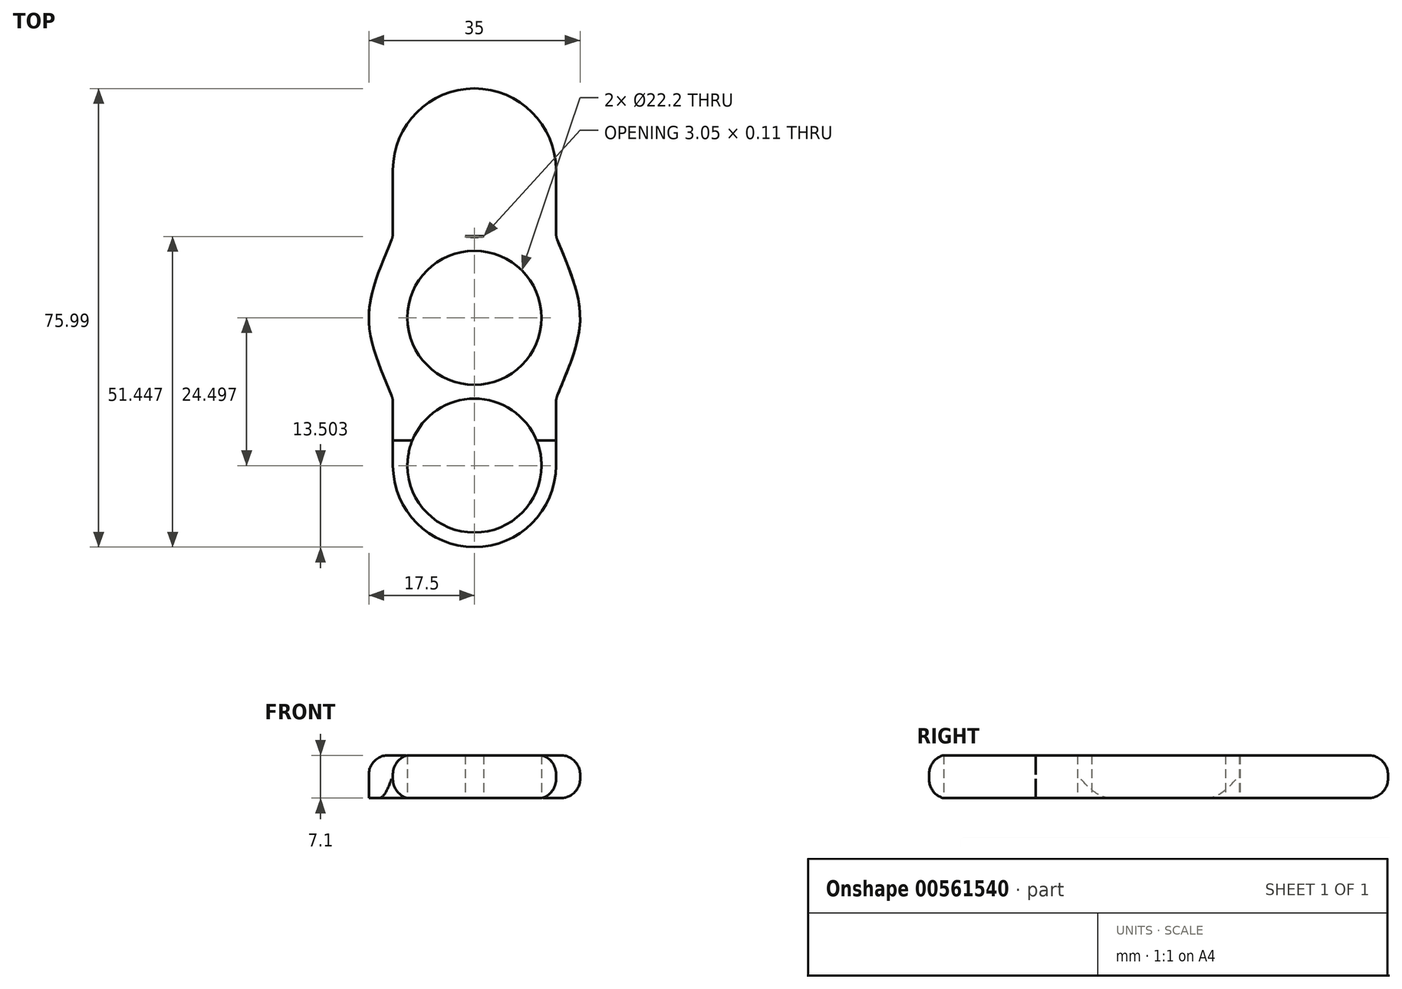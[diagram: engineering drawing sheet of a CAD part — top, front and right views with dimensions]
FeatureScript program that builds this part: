
annotation { "Feature Type Name" : "Feature", "Feature Type Description" : "" }
export const myFeature = defineFeature(function(context is Context, id is Id, definition is map)
    precondition{}
    {
        {
            var Q0;
            Q0=qCreatedBy(makeId("Top.planeOp"),FACE);
            var sketch = newSketch(context, id + "F0", { "sketchPlane" : qUnion([Q0])});
            skCircle(sketch, "E0", {"center": v(0, 0) * mm, "radius": 11.1 * mm});
            skCircle(sketch, "E1.cCircle", {"center": v(0, 0) * mm, "radius": 13.5 * mm, "construction": true});
            skLineSegment(sketch, "E1.0", {"start": v(13.5, 13.5) * mm, "end": v(13.5, -13.5) * mm});
            skLineSegment(sketch, "E1.1", {"start": v(13.5, -13.5) * mm, "end": v(-13.5, -13.5) * mm});
            skLineSegment(sketch, "E1.2", {"start": v(-13.5, -13.5) * mm, "end": v(-13.5, 13.5) * mm});
            skLineSegment(sketch, "E1.3", {"start": v(-13.5, 13.5) * mm, "end": v(13.5, 13.5) * mm});
            skPoint(sketch, "E1.0.midPoint", {"position": v(13.5, 0) * mm});
            skCircle(sketch, "E2", {"center": v(0, 24.5) * mm, "radius": 11.1 * mm});
            skPoint(sketch, "E2.centerSnap0", {"position": v(0, 13.5) * mm});
            skCircle(sketch, "E3", {"center": v(0, -24.5) * mm, "radius": 11.1 * mm});
            skLineSegment(sketch, "E4.top", {"start": v(-13.5, 24.5) * mm, "end": v(13.5, 24.5) * mm});
            skLineSegment(sketch, "E4.left", {"start": v(-13.5, 13.5) * mm, "end": v(-13.5, 24.5) * mm});
            skLineSegment(sketch, "E4.right", {"start": v(13.5, 13.5) * mm, "end": v(13.5, 24.5) * mm});
            skLineSegment(sketch, "E5.bottom", {"start": v(-13.5, -13.5) * mm, "end": v(13.5, -13.5) * mm});
            skLineSegment(sketch, "E5.top", {"start": v(-13.5, -24.5) * mm, "end": v(13.5, -24.5) * mm});
            skLineSegment(sketch, "E5.left", {"start": v(-13.5, -13.5) * mm, "end": v(-13.5, -24.5) * mm});
            skLineSegment(sketch, "E5.right", {"start": v(13.5, -13.5) * mm, "end": v(13.5, -24.5) * mm});
            skArc(sketch, "E6", {"start": v(-13.5, -24.5) * mm, "mid": v(0, -38) * mm, "end": v(13.5, -24.5) * mm});
            skArc(sketch, "E7", {"start": v(13.5, 24.5) * mm, "mid": v(0, 38) * mm, "end": v(-13.5, 24.5) * mm});
            skFitSpline(sketch, "E8", {"points": [v(13.5, 13.5) * mm, v(17.5, 0) * mm, v(13.5, -13.5) * mm], "startDerivative": vector(10.46, -27) * mm, "endDerivative": vector(-10.46, -27) * mm});
            skFitSpline(sketch, "E9", {"points": [v(-13.5, 13.5) * mm, v(-17.5, 0) * mm, v(-13.5, -13.5) * mm], "startDerivative": vector(-10.46, -27) * mm, "endDerivative": vector(10.46, -27) * mm});
            skSolve(sketch);
        }
        {
            var Q0;
            {var subQ4=sQuery(id+"F0.wireOp",EDGE,"E7");Q0=makeQuery(id+"F0.imprint","IMPRINT",FACE,{"disambiguationData":[TD([[makeQuery(id+"F0.imprint","IMPRINT",EDGE,{"derivedFrom":subQ4}),1.0]])]});}
            var Q1;
            {var subQ5=sQuery(id+"F0.wireOp",EDGE,"E4.left");Q1=makeQuery(id+"F0.imprint","IMPRINT",FACE,{"disambiguationData":[TD([[makeQuery(id+"F0.imprint","IMPRINT",EDGE,{"derivedFrom":subQ5}),-1.0]])]});}
            var Q2;
            {var subQ5=sQuery(id+"F0.wireOp",EDGE,"E4.right");Q2=makeQuery(id+"F0.imprint","IMPRINT",FACE,{"disambiguationData":[TD([[makeQuery(id+"F0.imprint","IMPRINT",EDGE,{"derivedFrom":subQ5}),1.0]])]});}
            var Q3;
            Q3=makeQuery(id+"F0.imprint","IMPRINT",FACE,{"disambiguationData":[TD([[makeQuery(id+"F0.imprint","IMPRINT",EDGE,{"derivedFrom":sQuery(id+"F0.wireOp",EDGE,"E0")}),-1.0]])]});
            var Q4;
            Q4=makeQuery(id+"F0.imprint","IMPRINT",FACE,{"disambiguationData":[TD([[makeQuery(id+"F0.imprint","IMPRINT",EDGE,{"derivedFrom":sQuery(id+"F0.wireOp",EDGE,"E1.0")}),1.0]])]});
            var Q5;
            Q5=makeQuery(id+"F0.imprint","IMPRINT",FACE,{"disambiguationData":[TD([[makeQuery(id+"F0.imprint","IMPRINT",EDGE,{"derivedFrom":sQuery(id+"F0.wireOp",EDGE,"E1.2")}),1.0]])]});
            var Q6;
            {var subQ5=sQuery(id+"F0.wireOp",EDGE,"E5.left");Q6=makeQuery(id+"F0.imprint","IMPRINT",FACE,{"disambiguationData":[TD([[makeQuery(id+"F0.imprint","IMPRINT",EDGE,{"derivedFrom":subQ5}),1.0]])]});}
            var Q7;
            {var subQ5=sQuery(id+"F0.wireOp",EDGE,"E5.right");Q7=makeQuery(id+"F0.imprint","IMPRINT",FACE,{"disambiguationData":[TD([[makeQuery(id+"F0.imprint","IMPRINT",EDGE,{"derivedFrom":subQ5}),-1.0]])]});}
            var Q8;
            {var subQ4=sQuery(id+"F0.wireOp",EDGE,"E6");Q8=makeQuery(id+"F0.imprint","IMPRINT",FACE,{"disambiguationData":[TD([[makeQuery(id+"F0.imprint","IMPRINT",EDGE,{"derivedFrom":subQ4}),1.0]])]});}
            var Q9;
            {var subQ0=sQuery(id+"F0.wireOp",EDGE,"E4.top");var subQ1=sQuery(id+"F0.wireOp",EDGE,"E2");var subQ2=makeQuery(id+"F0.imprint","INTERSECT",VERTEX,{"disambiguationData":[OD(0.0)],"derivedFrom":[subQ1,subQ0]});Q9=makeQuery(id+"F0.imprint","IMPRINT",FACE,{"disambiguationData":[TD([[makeQuery(id+"F0.imprint","IMPRINT",EDGE,{"disambiguationData":[TD([[subQ2,1.0]])],"derivedFrom":subQ1}),1.0]])]});}
            var Q10;
            {var subQ0=sQuery(id+"F0.wireOp",EDGE,"E4.top");var subQ1=sQuery(id+"F0.wireOp",EDGE,"E2");var subQ2=makeQuery(id+"F0.imprint","INTERSECT",VERTEX,{"disambiguationData":[OD(0.0)],"derivedFrom":[subQ1,subQ0]});Q10=makeQuery(id+"F0.imprint","IMPRINT",FACE,{"disambiguationData":[TD([[makeQuery(id+"F0.imprint","IMPRINT",EDGE,{"disambiguationData":[TD([[subQ2,-1.0]])],"derivedFrom":subQ1}),1.0]])]});}
            var Q11;
            {var subQ0=sQuery(id+"F0.wireOp",EDGE,"E1.3");var subQ1=sQuery(id+"F0.wireOp",EDGE,"E2");var subQ2=makeQuery(id+"F0.imprint","INTERSECT",VERTEX,{"disambiguationData":[OD(0.0)],"derivedFrom":[subQ1,subQ0]});Q11=makeQuery(id+"F0.imprint","IMPRINT",FACE,{"disambiguationData":[TD([[makeQuery(id+"F0.imprint","IMPRINT",EDGE,{"disambiguationData":[TD([[subQ2,-1.0]])],"derivedFrom":subQ1}),1.0]])]});}
            extrude(context, id + "F1", {"entities" : qUnion([Q0, Q1, Q2, Q3, Q4, Q5, Q6, Q7, Q8, Q9, Q10, Q11]), "depth" : 7.1 * mm, "offsetDistance" : 25 * mm});
        }
        {
            var Q0;
            Q0=makeQuery(id+"F1.opExtrude","SWEPT_EDGE",EDGE,{"disambiguationData":[OSD([sQuery(id+"F0.wireOp",EDGE,"E1.0"),sQuery(id+"F0.wireOp",EDGE,"E5.bottom"),sQuery(id+"F0.wireOp",EDGE,"E5.right"),sQuery(id+"F0.wireOp",EDGE,"E8")])]});
            var Q1;
            Q1=makeQuery(id+"F1.opExtrude","CAP_EDGE",EDGE,{"disambiguationData":[OSD([sQuery(id+"F0.wireOp",EDGE,"E8")])],"isStart":false});
            var Q2;
            Q2=makeQuery(id+"F1.opExtrude","CAP_EDGE",EDGE,{"disambiguationData":[OSD([sQuery(id+"F0.wireOp",EDGE,"E8")])],"isStart":true});
            var Q3;
            Q3=makeQuery(id+"F1.opExtrude","SWEPT_EDGE",EDGE,{"disambiguationData":[OSD([sQuery(id+"F0.wireOp",EDGE,"E1.0"),sQuery(id+"F0.wireOp",EDGE,"E1.3"),sQuery(id+"F0.wireOp",EDGE,"E4.right"),sQuery(id+"F0.wireOp",EDGE,"E8")])]});
            var Q4;
            Q4=makeQuery(id+"F1.opExtrude","CAP_EDGE",EDGE,{"disambiguationData":[OSD([sQuery(id+"F0.wireOp",EDGE,"E4.right")])],"isStart":false});
            var Q5;
            Q5=makeQuery(id+"F1.opExtrude","CAP_EDGE",EDGE,{"disambiguationData":[OSD([sQuery(id+"F0.wireOp",EDGE,"E7")])],"isStart":false});
            var Q6;
            Q6=makeQuery(id+"F1.opExtrude","CAP_EDGE",EDGE,{"disambiguationData":[OSD([sQuery(id+"F0.wireOp",EDGE,"E7")])],"isStart":true});
            var Q7;
            Q7=makeQuery(id+"F1.opExtrude","SWEPT_FACE",FACE,{"disambiguationData":[OSD([sQuery(id+"F0.wireOp",EDGE,"E4.right")])]});
            var Q8;
            Q8=makeQuery(id+"F1.opExtrude","CAP_EDGE",EDGE,{"disambiguationData":[OSD([sQuery(id+"F0.wireOp",EDGE,"E4.left")])],"isStart":false});
            var Q9;
            Q9=makeQuery(id+"F1.opExtrude","CAP_EDGE",EDGE,{"disambiguationData":[OSD([sQuery(id+"F0.wireOp",EDGE,"E9")])],"isStart":false});
            var Q10;
            Q10=makeQuery(id+"F1.opExtrude","CAP_EDGE",EDGE,{"disambiguationData":[OSD([sQuery(id+"F0.wireOp",EDGE,"E6")])],"isStart":false});
            var Q11;
            Q11=makeQuery(id+"F1.opExtrude","CAP_EDGE",EDGE,{"disambiguationData":[OSD([sQuery(id+"F0.wireOp",EDGE,"E5.left")])],"isStart":false});
            var Q12;
            Q12=makeQuery(id+"F1.opExtrude","CAP_EDGE",EDGE,{"disambiguationData":[OSD([sQuery(id+"F0.wireOp",EDGE,"E5.right")])],"isStart":false});
            var Q13;
            Q13=makeQuery(id+"F1.opExtrude","CAP_EDGE",EDGE,{"disambiguationData":[OSD([sQuery(id+"F0.wireOp",EDGE,"E5.right")])],"isStart":true});
            var Q14;
            Q14=makeQuery(id+"F1.opExtrude","CAP_EDGE",EDGE,{"disambiguationData":[OSD([sQuery(id+"F0.wireOp",EDGE,"E6")])],"isStart":true});
            var Q15;
            Q15=makeQuery(id+"F1.opExtrude","SWEPT_EDGE",EDGE,{"disambiguationData":[OSD([sQuery(id+"F0.wireOp",EDGE,"E1.2"),sQuery(id+"F0.wireOp",EDGE,"E5.bottom"),sQuery(id+"F0.wireOp",EDGE,"E5.left"),sQuery(id+"F0.wireOp",EDGE,"E9")])]});
            var Q16;
            Q16=makeQuery(id+"F1.opExtrude","SWEPT_EDGE",EDGE,{"disambiguationData":[OSD([sQuery(id+"F0.wireOp",EDGE,"E1.2"),sQuery(id+"F0.wireOp",EDGE,"E1.3"),sQuery(id+"F0.wireOp",EDGE,"E4.left"),sQuery(id+"F0.wireOp",EDGE,"E9")])]});
            fillet(context, id + "F2", {"entities" : qUnion([Q0, Q1, Q2, Q3, Q4, Q5, Q6, Q7, Q8, Q9, Q10, Q11, Q12, Q13, Q14, Q15, Q16]), "radius" : 3.2 * mm, "tangentPropagation" : true, "allowEdgeOverflow" : false});
        }
    });
